# Revit family: MKH1-350(500)R3(R4)
name_source: partatom
category: Mechanical Equipment
revit_build: Autodesk Revit 2013 (Build: 20120221_2030(x64)
units: mm (PartAtom-declared; Revit-internal decimal feet)

## types (4) — shared parameters
Circuit breaker = 15 A
Condensation = water
Depth = 1240 mm
Description = High efficiency water cooled
Drain pipe = 18.5 mm
Installation = Indoor installation
Liquid pipe = 19.05 mm  [stored 0.0625 ft]
Machine material = Galvanized Steel
Manufacturer = Midea
Panel color = WH101
Power supply = 220-240V ~50Hz/60Hz
Rated current = 0 A
Series = FCU
Width = 495 mm
clearance access behind = 50 mm  [stored 0.164042 ft]
clearance access down = 90 mm
clearance access left = 150 mm
clearance access right = 150 mm
clearance access up = 1500 mm  [stored 4.92126 ft]

## per-type parameters (varying)
| type | Air Flow(H/M/L) | Cooling Capacity(H/M/L) | Heating Capacity(H/M/L) | Height | Net Weight | Power Input(H/M/L) |
| MKH1-350-R3 | 595/447/319 m3/h | 3.85/3.19/2.46 kW | 3.70/2.97/2.25 kW | 211 mm | 24.00 kg | 51/32/19 W |
| MKH1-350-R4 | 595/450/319 m3/h | 4.20/3.38/2.48 kW | 4.10/3.25/2.39 kW | 211 mm | 25.40 kg | 51/32/19 W |
| MKH1-500-R3 | 790/560/392 m3/h | 4.65/3.80/2.92 kW | 4.35/3.44/2.62 kW | 211 mm | 25.50 kg | 91/54/34 W |
| MKH1-500-R4 | 800/574/404 m3/h | 5.35/4.25/3.31 kW | 5.70/4.36/3.22 kW | 200 mm | 26.30 kg | 91/54/35 W |

note: column(s) folded — value = type name in every type: Model

note: [stored X ft] marks values corroborated as IEEE doubles in the binary element streams (Revit-internal decimal feet)

## geometry (parser evidence)
native form markers: Sweep x5
no freeform markers — native parametric forms only
